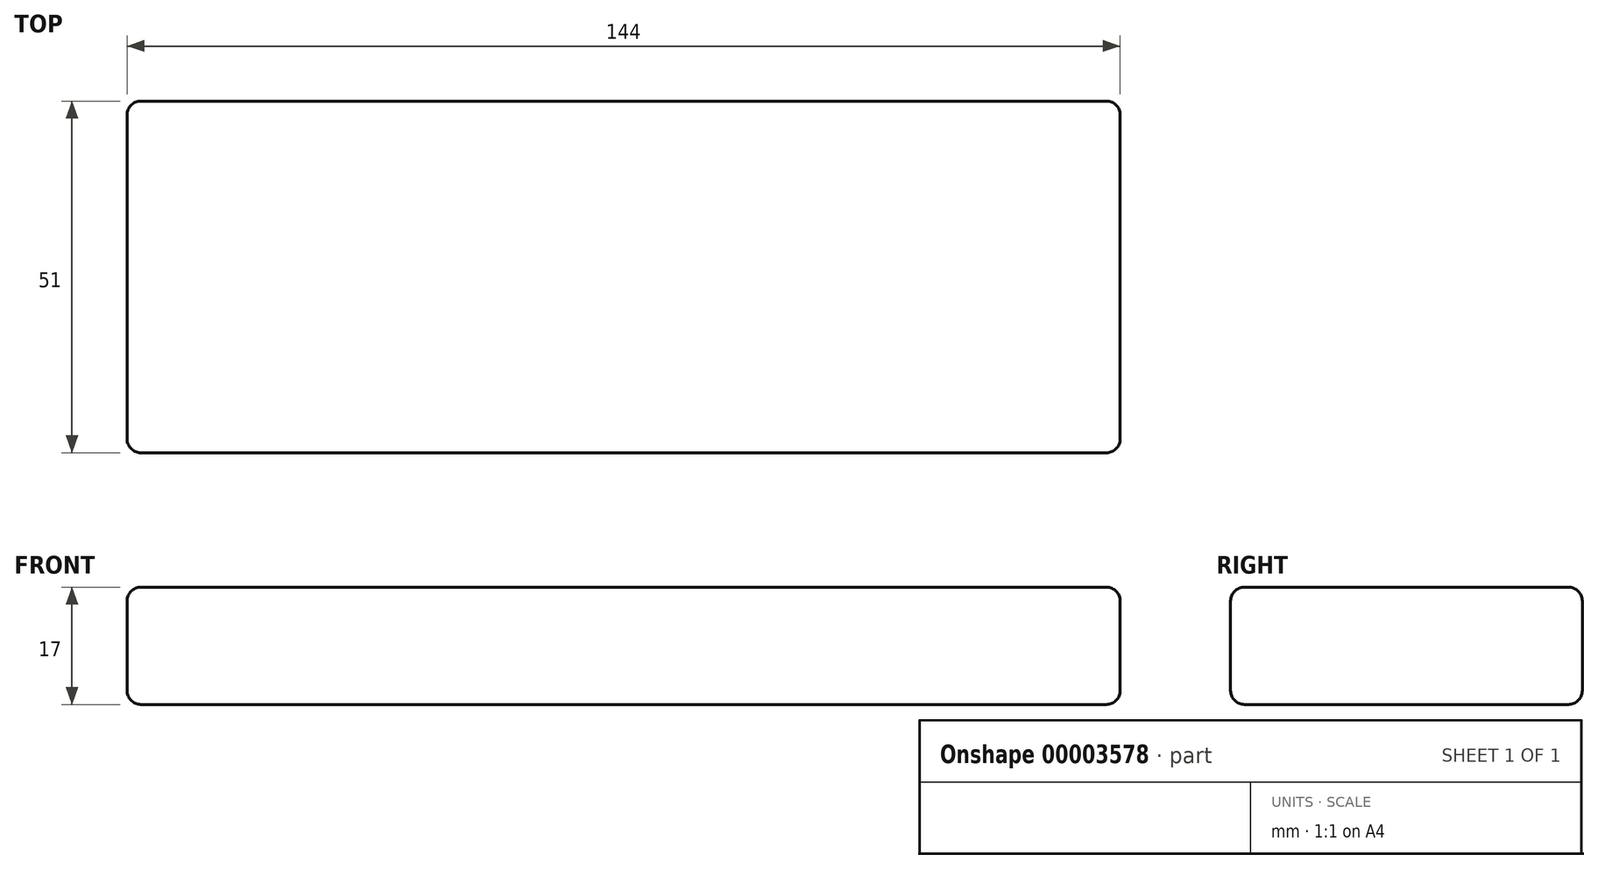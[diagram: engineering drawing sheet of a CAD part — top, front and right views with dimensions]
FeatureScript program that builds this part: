
annotation { "Feature Type Name" : "Feature", "Feature Type Description" : "" }
export const myFeature = defineFeature(function(context is Context, id is Id, definition is map)
    precondition{}
    {
        {
            var Q0;
            Q0=qCreatedBy(makeId("Top.planeOp"),FACE);
            var sketch = newSketch(context, id + "F0", { "sketchPlane" : qUnion([Q0])});
            skLineSegment(sketch, "E0.rect.bottom", {"start": v(70, -25.5) * mm, "end": v(-70, -25.5) * mm});
            skLineSegment(sketch, "E0.rect.top", {"start": v(70, 25.5) * mm, "end": v(-70, 25.5) * mm});
            skLineSegment(sketch, "E0.rect.left", {"start": v(72, -23.5) * mm, "end": v(72, 23.5) * mm});
            skLineSegment(sketch, "E0.rect.right", {"start": v(-72, -23.5) * mm, "end": v(-72, 23.5) * mm});
            skPoint(sketch, "E0.rect.middle", {"position": v(0, 0) * mm});
            skPoint(sketch, "E1.visualSharp", {"position": v(-72, 25.5) * mm});
            skArc(sketch, "E1.filletArc", {"start": v(-70, 25.5) * mm, "mid": v(-71.41, 24.91) * mm, "end": v(-72, 23.5) * mm});
            skPoint(sketch, "E2.visualSharp", {"position": v(72, 25.5) * mm});
            skArc(sketch, "E2.filletArc", {"start": v(72, 23.5) * mm, "mid": v(71.41, 24.91) * mm, "end": v(70, 25.5) * mm});
            skPoint(sketch, "E3.visualSharp", {"position": v(72, -25.5) * mm});
            skArc(sketch, "E3.filletArc", {"start": v(70, -25.5) * mm, "mid": v(71.41, -24.91) * mm, "end": v(72, -23.5) * mm});
            skPoint(sketch, "E4.visualSharp", {"position": v(-72, -25.5) * mm});
            skArc(sketch, "E4.filletArc", {"start": v(-72, -23.5) * mm, "mid": v(-71.41, -24.91) * mm, "end": v(-70, -25.5) * mm});
            skSolve(sketch);
        }
        {
            var Q0;
            Q0=makeQuery(id+"F0.imprint","IMPRINT",FACE,{"disambiguationData":[TD([[makeQuery(id+"F0.imprint","IMPRINT",EDGE,{"derivedFrom":sQuery(id+"F0.wireOp",EDGE,"E0.rect.bottom")}),-1.0]])]});
            extrude(context, id + "F1", {"entities" : qUnion([Q0]), "depth" : 17 * mm});
        }
        {
            var Q0;
            Q0=makeQuery(id+"F1.opExtrude","CAP_EDGE",EDGE,{"disambiguationData":[OSD([sQuery(id+"F0.wireOp",EDGE,"E0.rect.bottom")])],"isStart":false});
            var Q1;
            Q1=makeQuery(id+"F1.opExtrude","CAP_EDGE",EDGE,{"disambiguationData":[OSD([sQuery(id+"F0.wireOp",EDGE,"E0.rect.bottom")])],"isStart":true});
            fillet(context, id + "F2", {"entities" : qUnion([Q0, Q1]), "radius" : 2 * mm, "tangentPropagation" : true, "allowEdgeOverflow" : false});
        }
    });
